# Revit family: Toilet-Floor_Mount-KOHLER-Veil-K-1381_1
name_source: partatom
category: Plumbing Fixtures
units: mm (PartAtom-declared; Revit-internal decimal feet)

## family parameters
Cut with Voids When Loaded = No
Host = Face
Maintain Annotation Orientation = No
OmniClass Number = 23.31.19.00
OmniClass Title = Toilets
Part Type = Normal
Room Calculation Point = No
Round Connector Dimension = Use Diameter
Shared = No

## types (3) — shared parameters
ADA Compliant = No
Assembly Code = D2010100
Bowl Height = 15 3/8"
CW Connection = Yes
Cold Water Inlet = Cold Water Inlet
Date Modified = 07/28/2024
Default Elevation = 0"
Flow Rate = 0 GPM
HW Connection = No
Height = 26 7/8"
Hot Water Inlet = Hot Water Inlet
Length = 28 5/16"
Manufacturer = Kohler Co.
Master Format 2014 = 22 42 13.13
Master Format 2014 Name = Residential Water Closets
Material = Vitreous China
Pressure = 0.00 psi
Product Documentation Link = https://www.us.kohler.com
Product Name = Veil
Product Page URL = http://www.us.kohler.com
Rough-In = 12"
URL = https://www.us.kohler.com
Vent Connection = No
Waste Connection = Yes
Waste Water Outlet = Waste Water Outlet
WaterSense Certified = Yes
Width = 15 3/16"

## per-type parameters (varying)
| type | Description | Finish | Flush Rate- GPF | Flush Rate- LPF | Model | Seat Included | Type |
| Without Concealed Cords, 0-White | One-piece elongated dual-flush toilet with skirted trapway | Kohler-Vitreous_China-0-White | 0 | 0 | K-1381-0 | Yes | 1 |
| With Concealed Cords, 0-White | One-piece elongated dual-flush toilet with skirted trapway and concealed cords | Kohler-Vitreous_China-0-White | 0 | 0 | K-1381-HC-0 | No | 3 |
| Without Concealed Cords, 7-Black Black | One-piece elongated dual-flush toilet with skirted trapway | Kohler-Vitreous_China-7-Black_Black | 1.28 GPF | 4.8 LPF | K-1381-7 | Yes | 2 |

## geometry (parser evidence)
native form markers: Sweep x9
no freeform markers — native parametric forms only
